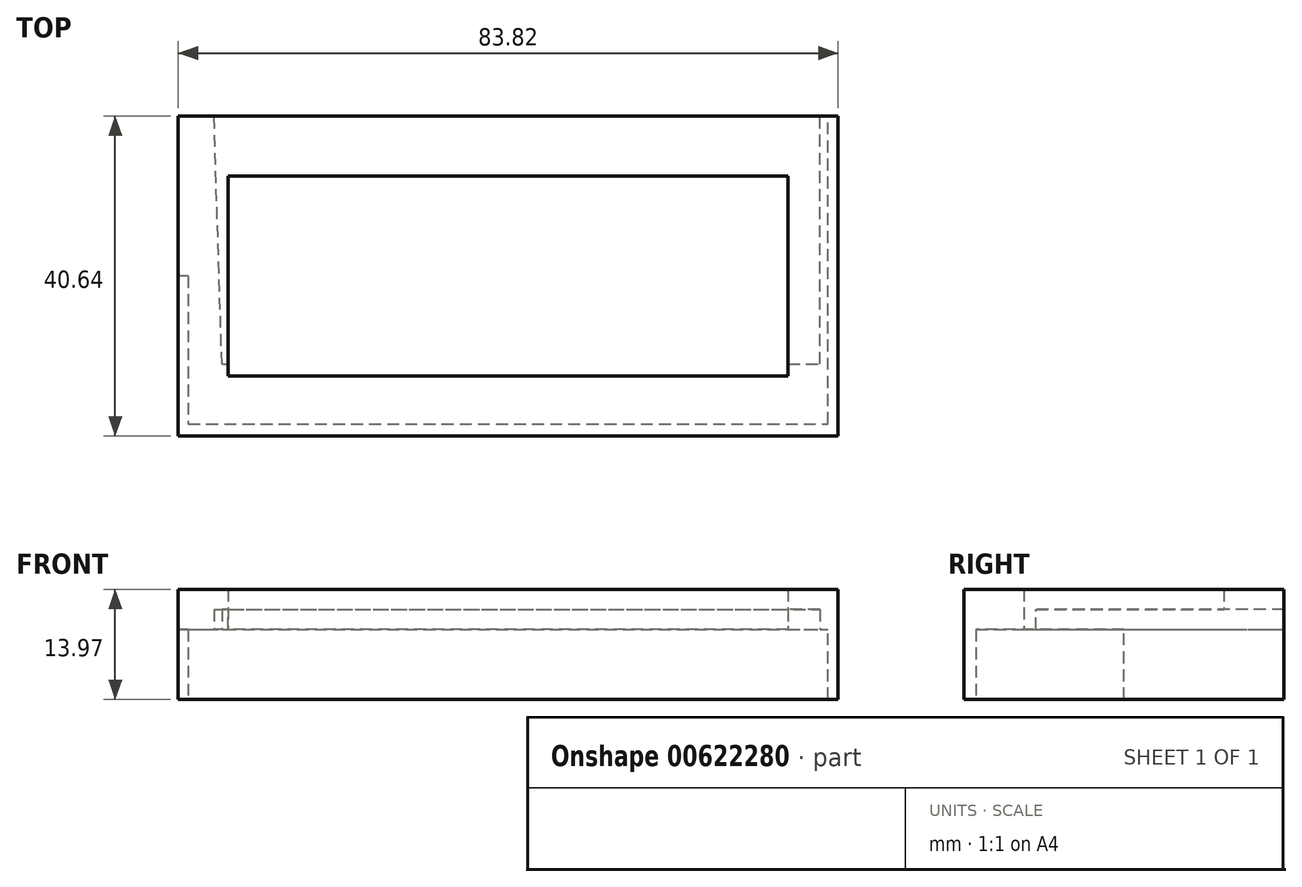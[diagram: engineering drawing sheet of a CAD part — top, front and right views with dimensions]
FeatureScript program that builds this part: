
annotation { "Feature Type Name" : "Feature", "Feature Type Description" : "" }
export const myFeature = defineFeature(function(context is Context, id is Id, definition is map)
    precondition{}
    {
        {
            var Q0;
            Q0=qCreatedBy(makeId("Top.planeOp"),FACE);
            var sketch = newSketch(context, id + "F0", { "sketchPlane" : qUnion([Q0])});
            skLineSegment(sketch, "E0", {"start": v(0, 0) * mm, "end": v(-35.56, 0) * mm});
            skLineSegment(sketch, "E1", {"start": v(-35.56, 0) * mm, "end": v(-35.56, 12.7) * mm});
            skLineSegment(sketch, "E2", {"start": v(-35.56, 12.7) * mm, "end": v(35.56, 12.7) * mm});
            skLineSegment(sketch, "E3", {"start": v(35.56, 12.7) * mm, "end": v(35.56, -12.7) * mm});
            skLineSegment(sketch, "E4", {"start": v(35.56, -12.7) * mm, "end": v(-35.56, -12.7) * mm});
            skLineSegment(sketch, "E5", {"start": v(-35.56, -12.7) * mm, "end": v(-35.56, 0) * mm});
            skSolve(sketch);
        }
        {
            var Q0;
            Q0=qCreatedBy(makeId("Top.planeOp"),FACE);
            var sketch = newSketch(context, id + "F1", { "sketchPlane" : qUnion([Q0])});
            skLineSegment(sketch, "E6", {"start": v(0, 0) * mm, "end": v(-41.91, 0) * mm});
            skLineSegment(sketch, "E7", {"start": v(-41.91, 0) * mm, "end": v(-41.91, 20.32) * mm});
            skLineSegment(sketch, "E8", {"start": v(-41.91, 20.32) * mm, "end": v(41.91, 20.32) * mm});
            skLineSegment(sketch, "E9", {"start": v(41.91, 20.32) * mm, "end": v(41.91, -20.32) * mm});
            skLineSegment(sketch, "E10", {"start": v(41.91, -20.32) * mm, "end": v(-41.91, -20.32) * mm});
            skLineSegment(sketch, "E11", {"start": v(-41.91, -20.32) * mm, "end": v(-41.91, 0) * mm});
            skSolve(sketch);
        }
        {
            var Q0;
            Q0 = qSketchRegion(id + "F1", true);
            extrude(context, id + "F2", {"entities" : qUnion([Q0]), "depth" : 25.4 * mm, "offsetDistance" : 25.4 * mm});
        }
        {
            var Q0;
            Q0 = qSketchRegion(id + "F0", true);
            extrude(context, id + "F3", {"entities" : qUnion([Q0]), "operationType" : NewBodyOperationType.REMOVE, "depth" : 25.4 * mm, "offsetDistance" : 25.4 * mm});
        }
        {
            var Q0;
            Q0=qCreatedBy(makeId("Top.planeOp"),FACE);
            var sketch = newSketch(context, id + "F4", { "sketchPlane" : qUnion([Q0])});
            skLineSegment(sketch, "E12", {"start": v(0, 0) * mm, "end": v(-40.64, 0) * mm});
            skLineSegment(sketch, "E13", {"start": v(-40.64, 0) * mm, "end": v(-40.64, -18.8) * mm});
            skLineSegment(sketch, "E14", {"start": v(-40.64, -18.8) * mm, "end": v(40.64, -18.8) * mm});
            skLineSegment(sketch, "E15", {"start": v(40.64, -18.8) * mm, "end": v(40.64, 18.8) * mm});
            skLineSegment(sketch, "E16", {"start": v(-40.64, 29.7) * mm, "end": v(40.64, 29.7) * mm});
            skLineSegment(sketch, "E17", {"start": v(40.64, 29.7) * mm, "end": v(40.64, 18.8) * mm});
            skLineSegment(sketch, "E18", {"start": v(0, 0) * mm, "end": v(-44.77, 0) * mm});
            skLineSegment(sketch, "E19", {"start": v(-44.77, 0) * mm, "end": v(-44.77, 29.85) * mm});
            skLineSegment(sketch, "E20", {"start": v(-44.77, 29.85) * mm, "end": v(-40.64, 29.7) * mm});
            skSolve(sketch);
        }
        {
            var Q0;
            Q0 = qSketchRegion(id + "F4", true);
            extrude(context, id + "F5", {"entities" : qUnion([Q0]), "operationType" : NewBodyOperationType.REMOVE, "depth" : 20.32 * mm, "offsetDistance" : 25.4 * mm});
        }
        {
            var Q0;
            Q0=qCreatedBy(makeId("Top.planeOp"),FACE);
            var sketch = newSketch(context, id + "F6", { "sketchPlane" : qUnion([Q0])});
            skLineSegment(sketch, "E21", {"start": v(39.61, 0) * mm, "end": v(39.61, -11.16) * mm});
            skLineSegment(sketch, "E22", {"start": v(39.61, -11.16) * mm, "end": v(35.11, -11.16) * mm});
            skLineSegment(sketch, "E23", {"start": v(35.11, -11.16) * mm, "end": v(35.11, 0) * mm});
            skLineSegment(sketch, "E24.MirrorCS", {"start": v(35.11, 11.16) * mm, "end": v(35.11, 0) * mm});
            skLineSegment(sketch, "E25.MirrorCS", {"start": v(39.61, 0) * mm, "end": v(39.61, 11.16) * mm});
            skLineSegment(sketch, "E26", {"start": v(35.11, 11.16) * mm, "end": v(35.11, 23.86) * mm});
            skLineSegment(sketch, "E27", {"start": v(39.61, 11.16) * mm, "end": v(39.61, 23.86) * mm});
            skLineSegment(sketch, "E28", {"start": v(39.61, 23.86) * mm, "end": v(35.11, 23.86) * mm});
            skLineSegment(sketch, "E29", {"start": v(35.11, -11.16) * mm, "end": v(-36.36, -11.16) * mm});
            skLineSegment(sketch, "E30", {"start": v(35.11, 23.86) * mm, "end": v(-37.48, 23.86) * mm});
            skLineSegment(sketch, "E31", {"start": v(-37.48, 23.86) * mm, "end": v(-36.36, -11.16) * mm});
            skSolve(sketch);
        }
        {
            var Q0;
            Q0 = qSketchRegion(id + "F6", true);
            extrude(context, id + "F7", {"entities" : qUnion([Q0]), "operationType" : NewBodyOperationType.REMOVE, "depth" : 22.83 * mm, "offsetDistance" : 25.4 * mm});
        }
        {
            var Q0;
            Q0=qCreatedBy(makeId("Top.planeOp"),FACE);
            var sketch = newSketch(context, id + "F8", { "sketchPlane" : qUnion([Q0])});
            skLineSegment(sketch, "E32", {"start": v(0, 0) * mm, "end": v(-44.7, 0) * mm});
            skLineSegment(sketch, "E33", {"start": v(-44.7, 0) * mm, "end": v(-44.7, 15.72) * mm});
            skLineSegment(sketch, "E34", {"start": v(-44.7, 15.72) * mm, "end": v(0, 15.72) * mm});
            skLineSegment(sketch, "E35", {"start": v(0, 15.72) * mm, "end": v(0, 0) * mm});
            skSolve(sketch);
        }
        {
            var Q0;
            Q0 = qSketchRegion(id + "F8", true);
            extrude(context, id + "F9", {"entities" : qUnion([Q0]), "operationType" : NewBodyOperationType.REMOVE, "depth" : 17.63 * mm, "offsetDistance" : 25.4 * mm});
        }
        {
            var Q0;
            Q0=qCreatedBy(makeId("Top.planeOp"),FACE);
            var sketch = newSketch(context, id + "F10", { "sketchPlane" : qUnion([Q0])});
            skLineSegment(sketch, "E36", {"start": v(-64.21, 0) * mm, "end": v(-64.21, -44.94) * mm});
            skLineSegment(sketch, "E37", {"start": v(-64.21, -44.94) * mm, "end": v(66.28, -44.94) * mm});
            skLineSegment(sketch, "E38", {"start": v(66.28, -44.94) * mm, "end": v(66.28, 49.27) * mm});
            skLineSegment(sketch, "E39", {"start": v(66.28, 49.27) * mm, "end": v(-63.65, 47.76) * mm});
            skLineSegment(sketch, "E40", {"start": v(-63.65, 47.76) * mm, "end": v(-64.21, 0) * mm});
            skSolve(sketch);
        }
        {
            var Q0;
            Q0 = qSketchRegion(id + "F10", true);
            extrude(context, id + "F11", {"entities" : qUnion([Q0]), "operationType" : NewBodyOperationType.REMOVE, "depth" : 11.43 * mm, "offsetDistance" : 25.4 * mm});
        }
    });
